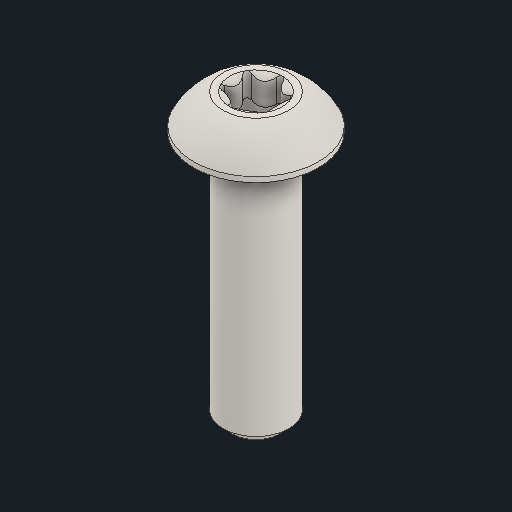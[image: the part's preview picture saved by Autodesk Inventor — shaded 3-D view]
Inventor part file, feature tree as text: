
AUTODESK INVENTOR PART (.ipt)
format: ipt  version: 2024 (Build 280153000, 153)  size: 176,128 bytes
history: native  units: in
note: dims shown in document units (in); Inventor stores cm internally (conversion verified against a paired STEP export)
features: chamfer x1
ambient origin geometry x8: Origin, YZ Plane, XZ Plane, XY Plane, X Axis, Y Axis, Z Axis, Center Point
bodies: Solid1 (feature_tree)
feature tree (1):
  chamfer  "Chamfer2"  [1 undecoded]
note: 1 required parameter value undecoded (feature->parameter linkage not recoverable at this tier; creation-order binding heuristic only, values carry confidence <= 0.55)
